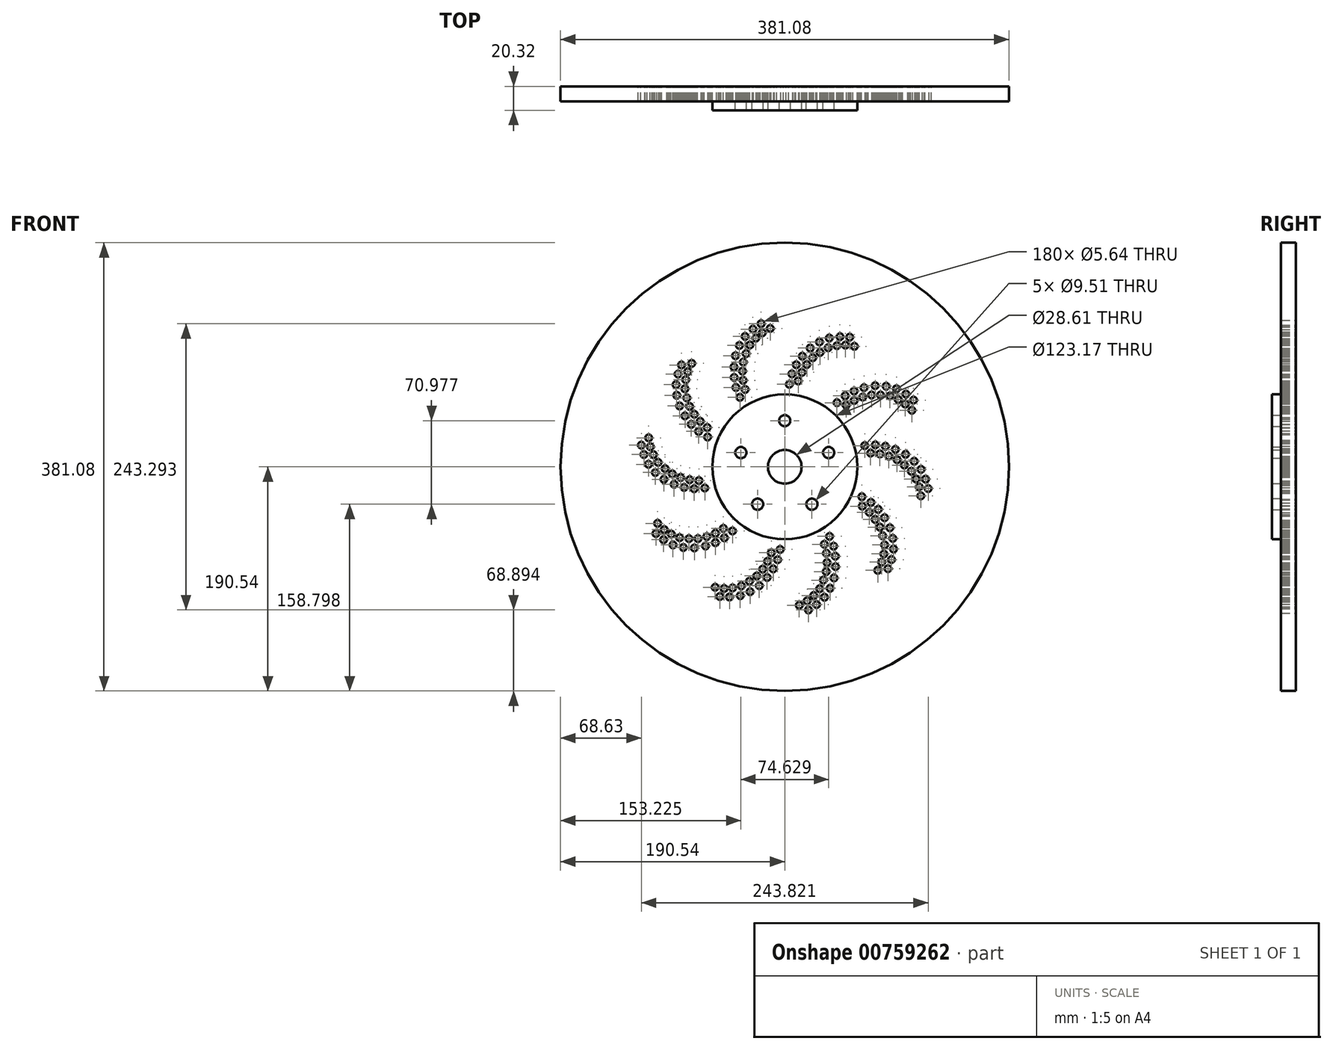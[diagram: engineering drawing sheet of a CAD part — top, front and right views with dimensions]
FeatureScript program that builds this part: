
annotation { "Feature Type Name" : "Feature", "Feature Type Description" : "" }
export const myFeature = defineFeature(function(context is Context, id is Id, definition is map)
    precondition{}
    {
        {
            var Q0;
            Q0=qCreatedBy(makeId("Front.planeOp"),FACE);
            var sketch = newSketch(context, id + "F0", { "sketchPlane" : qUnion([Q0])});
            skCircle(sketch, "E0", {"center": v(0, 0) * mm, "radius": 190.54 * mm});
            skCircle(sketch, "E1", {"center": v(0, 39.24) * mm, "radius": 4.75 * mm});
            skCircle(sketch, "E2.1.0", {"center": v(37.32, 12.13) * mm, "radius": 4.75 * mm});
            skCircle(sketch, "E2.2.0", {"center": v(23.06, -31.74) * mm, "radius": 4.75 * mm});
            skCircle(sketch, "E2.3.0", {"center": v(-23.06, -31.74) * mm, "radius": 4.75 * mm});
            skCircle(sketch, "E2.4.0", {"center": v(-37.31, 12.13) * mm, "radius": 4.75 * mm});
            skCircle(sketch, "E3", {"center": v(0, 0) * mm, "radius": 14.3 * mm});
            skCircle(sketch, "E4", {"center": v(0, 0) * mm, "radius": 61.59 * mm});
            skCircle(sketch, "E5", {"center": v(-38.12, 59.08) * mm, "radius": 2.82 * mm});
            skCircle(sketch, "E6.1.0", {"center": v(3.89, 70.2) * mm, "radius": 2.82 * mm});
            skCircle(sketch, "E6.2.0", {"center": v(44.4, 54.51) * mm, "radius": 2.82 * mm});
            skCircle(sketch, "E6.3.0", {"center": v(67.97, 18) * mm, "radius": 2.82 * mm});
            skCircle(sketch, "E6.4.0", {"center": v(65.57, -25.4) * mm, "radius": 2.82 * mm});
            skCircle(sketch, "E6.5.0", {"center": v(38.12, -59.08) * mm, "radius": 2.82 * mm});
            skCircle(sketch, "E6.6.0", {"center": v(-3.89, -70.2) * mm, "radius": 2.82 * mm});
            skCircle(sketch, "E6.7.0", {"center": v(-44.4, -54.51) * mm, "radius": 2.82 * mm});
            skCircle(sketch, "E6.8.0", {"center": v(-67.97, -18) * mm, "radius": 2.82 * mm});
            skCircle(sketch, "E6.9.0", {"center": v(-65.57, 25.4) * mm, "radius": 2.82 * mm});
            skLineSegment(sketch, "E6.anchor1", {"start": v(0, 0) * mm, "end": v(-38.12, 59.08) * mm, "construction": true});
            skLineSegment(sketch, "E6.anchor2", {"start": v(0, 0) * mm, "end": v(-65.57, 25.4) * mm, "construction": true});
            skLineSegment(sketch, "E7.anchor1", {"start": v(0, 0) * mm, "end": v(3.89, 70.2) * mm, "construction": true});
            skCircle(sketch, "E8.9.0", {"center": v(-41.5, 67.47) * mm, "radius": 2.82 * mm});
            skCircle(sketch, "E9.1.0", {"center": v(-73.23, 30.19) * mm, "radius": 2.82 * mm});
            skCircle(sketch, "E9.2.0", {"center": v(-77, -18.63) * mm, "radius": 2.82 * mm});
            skCircle(sketch, "E9.3.0", {"center": v(-51.34, -60.32) * mm, "radius": 2.82 * mm});
            skCircle(sketch, "E9.4.0", {"center": v(-6.08, -78.98) * mm, "radius": 2.82 * mm});
            skCircle(sketch, "E9.5.0", {"center": v(41.5, -67.47) * mm, "radius": 2.82 * mm});
            skCircle(sketch, "E9.6.0", {"center": v(73.23, -30.19) * mm, "radius": 2.82 * mm});
            skCircle(sketch, "E9.7.0", {"center": v(77, 18.63) * mm, "radius": 2.82 * mm});
            skCircle(sketch, "E9.8.0", {"center": v(51.34, 60.32) * mm, "radius": 2.82 * mm});
            skCircle(sketch, "E9.9.0", {"center": v(6.08, 78.98) * mm, "radius": 2.82 * mm});
            skCircle(sketch, "E10.9.0", {"center": v(-43.06, 75.98) * mm, "radius": 2.82 * mm});
            skCircle(sketch, "E11.1.0", {"center": v(-79.5, 36.16) * mm, "radius": 2.82 * mm});
            skCircle(sketch, "E11.2.0", {"center": v(-85.56, -17.47) * mm, "radius": 2.82 * mm});
            skCircle(sketch, "E11.3.0", {"center": v(-58.95, -64.43) * mm, "radius": 2.82 * mm});
            skCircle(sketch, "E11.4.0", {"center": v(-9.83, -86.78) * mm, "radius": 2.82 * mm});
            skCircle(sketch, "E11.5.0", {"center": v(43.06, -75.98) * mm, "radius": 2.82 * mm});
            skCircle(sketch, "E11.6.0", {"center": v(79.5, -36.16) * mm, "radius": 2.82 * mm});
            skCircle(sketch, "E11.7.0", {"center": v(85.56, 17.47) * mm, "radius": 2.82 * mm});
            skCircle(sketch, "E11.8.0", {"center": v(58.95, 64.43) * mm, "radius": 2.82 * mm});
            skCircle(sketch, "E11.9.0", {"center": v(9.83, 86.78) * mm, "radius": 2.82 * mm});
            skCircle(sketch, "E12.9.0", {"center": v(-43.16, 84.86) * mm, "radius": 2.82 * mm});
            skCircle(sketch, "E13.1.0", {"center": v(-84.8, 43.28) * mm, "radius": 2.82 * mm});
            skCircle(sketch, "E13.2.0", {"center": v(-94.04, -14.82) * mm, "radius": 2.82 * mm});
            skCircle(sketch, "E13.3.0", {"center": v(-67.37, -67.27) * mm, "radius": 2.82 * mm});
            skCircle(sketch, "E13.4.0", {"center": v(-14.96, -94.02) * mm, "radius": 2.82 * mm});
            skCircle(sketch, "E13.5.0", {"center": v(43.16, -84.86) * mm, "radius": 2.82 * mm});
            skCircle(sketch, "E13.6.0", {"center": v(84.8, -43.28) * mm, "radius": 2.82 * mm});
            skCircle(sketch, "E13.7.0", {"center": v(94.04, 14.82) * mm, "radius": 2.82 * mm});
            skCircle(sketch, "E13.8.0", {"center": v(67.37, 67.27) * mm, "radius": 2.82 * mm});
            skCircle(sketch, "E13.9.0", {"center": v(14.96, 94.02) * mm, "radius": 2.82 * mm});
            skCircle(sketch, "E14.9.0", {"center": v(-41.86, 94.41) * mm, "radius": 2.82 * mm});
            skCircle(sketch, "E15.9.0", {"center": v(-38.55, 103.18) * mm, "radius": 2.82 * mm});
            skCircle(sketch, "E16.1.0", {"center": v(-91.84, 60.81) * mm, "radius": 2.82 * mm});
            skCircle(sketch, "E16.2.0", {"center": v(-110.04, -4.78) * mm, "radius": 2.82 * mm});
            skCircle(sketch, "E16.3.0", {"center": v(-86.22, -68.55) * mm, "radius": 2.82 * mm});
            skCircle(sketch, "E16.4.0", {"center": v(-29.46, -106.13) * mm, "radius": 2.82 * mm});
            skCircle(sketch, "E16.5.0", {"center": v(38.55, -103.18) * mm, "radius": 2.82 * mm});
            skCircle(sketch, "E16.6.0", {"center": v(91.84, -60.81) * mm, "radius": 2.82 * mm});
            skCircle(sketch, "E16.7.0", {"center": v(110.04, 4.78) * mm, "radius": 2.82 * mm});
            skCircle(sketch, "E16.8.0", {"center": v(86.22, 68.55) * mm, "radius": 2.82 * mm});
            skCircle(sketch, "E16.9.0", {"center": v(29.46, 106.13) * mm, "radius": 2.82 * mm});
            skCircle(sketch, "E17.1.0", {"center": v(-89.36, 51.78) * mm, "radius": 2.82 * mm});
            skCircle(sketch, "E17.2.0", {"center": v(-102.73, -10.64) * mm, "radius": 2.82 * mm});
            skCircle(sketch, "E17.3.0", {"center": v(-76.86, -68.99) * mm, "radius": 2.82 * mm});
            skCircle(sketch, "E17.4.0", {"center": v(-21.63, -100.99) * mm, "radius": 2.82 * mm});
            skCircle(sketch, "E17.5.0", {"center": v(41.86, -94.41) * mm, "radius": 2.82 * mm});
            skCircle(sketch, "E17.6.0", {"center": v(89.36, -51.78) * mm, "radius": 2.82 * mm});
            skCircle(sketch, "E17.7.0", {"center": v(102.73, 10.64) * mm, "radius": 2.82 * mm});
            skCircle(sketch, "E17.8.0", {"center": v(76.86, 68.99) * mm, "radius": 2.82 * mm});
            skCircle(sketch, "E17.9.0", {"center": v(21.63, 100.99) * mm, "radius": 2.82 * mm});
            skCircle(sketch, "E18.9.0", {"center": v(-33.74, 110.84) * mm, "radius": 2.82 * mm});
            skCircle(sketch, "E19.1.0", {"center": v(-92.45, 69.84) * mm, "radius": 2.82 * mm});
            skCircle(sketch, "E19.2.0", {"center": v(-115.84, 2.16) * mm, "radius": 2.82 * mm});
            skCircle(sketch, "E19.3.0", {"center": v(-94.99, -66.34) * mm, "radius": 2.82 * mm});
            skCircle(sketch, "E19.4.0", {"center": v(-37.85, -109.5) * mm, "radius": 2.82 * mm});
            skCircle(sketch, "E19.5.0", {"center": v(33.74, -110.84) * mm, "radius": 2.82 * mm});
            skCircle(sketch, "E19.6.0", {"center": v(92.45, -69.84) * mm, "radius": 2.82 * mm});
            skCircle(sketch, "E19.7.0", {"center": v(115.84, -2.16) * mm, "radius": 2.82 * mm});
            skCircle(sketch, "E19.8.0", {"center": v(94.99, 66.34) * mm, "radius": 2.82 * mm});
            skCircle(sketch, "E19.9.0", {"center": v(37.85, 109.5) * mm, "radius": 2.82 * mm});
            skCircle(sketch, "E20.9.0", {"center": v(-27.05, 117.1) * mm, "radius": 2.82 * mm});
            skCircle(sketch, "E21.1.0", {"center": v(-90.7, 78.84) * mm, "radius": 2.82 * mm});
            skCircle(sketch, "E21.2.0", {"center": v(-119.72, 10.46) * mm, "radius": 2.82 * mm});
            skCircle(sketch, "E21.3.0", {"center": v(-103, -61.9) * mm, "radius": 2.82 * mm});
            skCircle(sketch, "E21.4.0", {"center": v(-46.95, -110.63) * mm, "radius": 2.82 * mm});
            skCircle(sketch, "E21.5.0", {"center": v(27.05, -117.1) * mm, "radius": 2.82 * mm});
            skCircle(sketch, "E21.6.0", {"center": v(90.7, -78.84) * mm, "radius": 2.82 * mm});
            skCircle(sketch, "E21.7.0", {"center": v(119.72, -10.46) * mm, "radius": 2.82 * mm});
            skCircle(sketch, "E21.8.0", {"center": v(103, 61.9) * mm, "radius": 2.82 * mm});
            skCircle(sketch, "E21.9.0", {"center": v(46.95, 110.63) * mm, "radius": 2.82 * mm});
            skCircle(sketch, "E22.9.0", {"center": v(-20.12, 121.65) * mm, "radius": 2.82 * mm});
            skCircle(sketch, "E23.1.0", {"center": v(-87.78, 86.59) * mm, "radius": 2.82 * mm});
            skCircle(sketch, "E23.2.0", {"center": v(-121.91, 18.45) * mm, "radius": 2.82 * mm});
            skCircle(sketch, "E23.3.0", {"center": v(-109.47, -56.73) * mm, "radius": 2.82 * mm});
            skCircle(sketch, "E23.4.0", {"center": v(-55.22, -110.24) * mm, "radius": 2.82 * mm});
            skCircle(sketch, "E23.5.0", {"center": v(20.12, -121.65) * mm, "radius": 2.82 * mm});
            skCircle(sketch, "E23.6.0", {"center": v(87.78, -86.59) * mm, "radius": 2.82 * mm});
            skCircle(sketch, "E23.7.0", {"center": v(121.91, -18.45) * mm, "radius": 2.82 * mm});
            skCircle(sketch, "E23.8.0", {"center": v(109.47, 56.73) * mm, "radius": 2.82 * mm});
            skCircle(sketch, "E23.9.0", {"center": v(55.22, 110.24) * mm, "radius": 2.82 * mm});
            skCircle(sketch, "E24.9.0", {"center": v(-33.66, 65.79) * mm, "radius": 2.82 * mm});
            skCircle(sketch, "E25.9.0", {"center": v(-35.41, 73.5) * mm, "radius": 2.82 * mm});
            skCircle(sketch, "E26.9.0", {"center": v(-35.92, 81.34) * mm, "radius": 2.82 * mm});
            skCircle(sketch, "E27.9.0", {"center": v(-35.26, 89) * mm, "radius": 2.82 * mm});
            skCircle(sketch, "E28.9.0", {"center": v(-32.86, 96.27) * mm, "radius": 2.82 * mm});
            skCircle(sketch, "E29.9.0", {"center": v(-29.65, 103.57) * mm, "radius": 2.82 * mm});
            skCircle(sketch, "E30.9.0", {"center": v(-24.62, 109.4) * mm, "radius": 2.82 * mm});
            skCircle(sketch, "E31.9.0", {"center": v(-19.06, 113.94) * mm, "radius": 2.82 * mm});
            skCircle(sketch, "E32.9.0", {"center": v(-12.3, 117.63) * mm, "radius": 2.82 * mm});
            skCircle(sketch, "E33.1.0", {"center": v(-65.9, 33.44) * mm, "radius": 2.82 * mm});
            skCircle(sketch, "E33.2.0", {"center": v(-72.97, -11.68) * mm, "radius": 2.82 * mm});
            skCircle(sketch, "E33.3.0", {"center": v(-52.17, -52.34) * mm, "radius": 2.82 * mm});
            skCircle(sketch, "E33.4.0", {"center": v(-11.44, -73) * mm, "radius": 2.82 * mm});
            skCircle(sketch, "E33.5.0", {"center": v(33.66, -65.79) * mm, "radius": 2.82 * mm});
            skCircle(sketch, "E33.6.0", {"center": v(65.9, -33.44) * mm, "radius": 2.82 * mm});
            skCircle(sketch, "E33.7.0", {"center": v(72.97, 11.68) * mm, "radius": 2.82 * mm});
            skCircle(sketch, "E33.8.0", {"center": v(52.17, 52.34) * mm, "radius": 2.82 * mm});
            skCircle(sketch, "E33.9.0", {"center": v(11.44, 73) * mm, "radius": 2.82 * mm});
            skCircle(sketch, "E34.1.0", {"center": v(-71.85, 38.65) * mm, "radius": 2.82 * mm});
            skCircle(sketch, "E34.2.0", {"center": v(-80.84, -10.97) * mm, "radius": 2.82 * mm});
            skCircle(sketch, "E34.3.0", {"center": v(-58.96, -56.39) * mm, "radius": 2.82 * mm});
            skCircle(sketch, "E34.4.0", {"center": v(-14.55, -80.27) * mm, "radius": 2.82 * mm});
            skCircle(sketch, "E34.5.0", {"center": v(35.41, -73.5) * mm, "radius": 2.82 * mm});
            skCircle(sketch, "E34.6.0", {"center": v(71.85, -38.65) * mm, "radius": 2.82 * mm});
            skCircle(sketch, "E34.7.0", {"center": v(80.84, 10.97) * mm, "radius": 2.82 * mm});
            skCircle(sketch, "E34.8.0", {"center": v(58.96, 56.39) * mm, "radius": 2.82 * mm});
            skCircle(sketch, "E34.9.0", {"center": v(14.55, 80.27) * mm, "radius": 2.82 * mm});
            skCircle(sketch, "E35.1.0", {"center": v(-76.87, 44.69) * mm, "radius": 2.82 * mm});
            skCircle(sketch, "E35.2.0", {"center": v(-88.46, -9.03) * mm, "radius": 2.82 * mm});
            skCircle(sketch, "E35.3.0", {"center": v(-66.26, -59.3) * mm, "radius": 2.82 * mm});
            skCircle(sketch, "E35.4.0", {"center": v(-18.75, -86.92) * mm, "radius": 2.82 * mm});
            skCircle(sketch, "E35.5.0", {"center": v(35.92, -81.34) * mm, "radius": 2.82 * mm});
            skCircle(sketch, "E35.6.0", {"center": v(76.87, -44.69) * mm, "radius": 2.82 * mm});
            skCircle(sketch, "E35.7.0", {"center": v(88.46, 9.03) * mm, "radius": 2.82 * mm});
            skCircle(sketch, "E35.8.0", {"center": v(66.26, 59.3) * mm, "radius": 2.82 * mm});
            skCircle(sketch, "E35.9.0", {"center": v(18.75, 86.92) * mm, "radius": 2.82 * mm});
            skCircle(sketch, "E36.1.0", {"center": v(-83.17, 58.57) * mm, "radius": 2.82 * mm});
            skCircle(sketch, "E36.1.1", {"center": v(-80.84, 51.29) * mm, "radius": 2.82 * mm});
            skCircle(sketch, "E36.1.2", {"center": v(-84.21, 74.03) * mm, "radius": 2.82 * mm});
            skCircle(sketch, "E36.1.3", {"center": v(-84.86, 66.36) * mm, "radius": 2.82 * mm});
            skCircle(sketch, "E36.2.0", {"center": v(-101.71, -1.5) * mm, "radius": 2.82 * mm});
            skCircle(sketch, "E36.2.1", {"center": v(-95.55, -6.02) * mm, "radius": 2.82 * mm});
            skCircle(sketch, "E36.2.2", {"center": v(-111.64, 10.4) * mm, "radius": 2.82 * mm});
            skCircle(sketch, "E36.2.3", {"center": v(-107.66, 3.8) * mm, "radius": 2.82 * mm});
            skCircle(sketch, "E36.3.0", {"center": v(-81.4, -61) * mm, "radius": 2.82 * mm});
            skCircle(sketch, "E36.3.1", {"center": v(-73.76, -61.04) * mm, "radius": 2.82 * mm});
            skCircle(sketch, "E36.3.2", {"center": v(-96.43, -57.22) * mm, "radius": 2.82 * mm});
            skCircle(sketch, "E36.3.3", {"center": v(-89.34, -60.2) * mm, "radius": 2.82 * mm});
            skCircle(sketch, "E36.4.0", {"center": v(-30, -97.2) * mm, "radius": 2.82 * mm});
            skCircle(sketch, "E36.4.1", {"center": v(-23.8, -92.73) * mm, "radius": 2.82 * mm});
            skCircle(sketch, "E36.4.2", {"center": v(-44.38, -102.97) * mm, "radius": 2.82 * mm});
            skCircle(sketch, "E36.4.3", {"center": v(-36.9, -101.22) * mm, "radius": 2.82 * mm});
            skCircle(sketch, "E36.5.0", {"center": v(32.86, -96.27) * mm, "radius": 2.82 * mm});
            skCircle(sketch, "E36.5.1", {"center": v(35.26, -89) * mm, "radius": 2.82 * mm});
            skCircle(sketch, "E36.5.2", {"center": v(24.62, -109.4) * mm, "radius": 2.82 * mm});
            skCircle(sketch, "E36.5.3", {"center": v(29.65, -103.57) * mm, "radius": 2.82 * mm});
            skCircle(sketch, "E36.6.0", {"center": v(83.17, -58.57) * mm, "radius": 2.82 * mm});
            skCircle(sketch, "E36.6.1", {"center": v(80.84, -51.29) * mm, "radius": 2.82 * mm});
            skCircle(sketch, "E36.6.2", {"center": v(84.21, -74.03) * mm, "radius": 2.82 * mm});
            skCircle(sketch, "E36.6.3", {"center": v(84.86, -66.36) * mm, "radius": 2.82 * mm});
            skCircle(sketch, "E36.7.0", {"center": v(101.71, 1.5) * mm, "radius": 2.82 * mm});
            skCircle(sketch, "E36.7.1", {"center": v(95.55, 6.02) * mm, "radius": 2.82 * mm});
            skCircle(sketch, "E36.7.2", {"center": v(111.64, -10.4) * mm, "radius": 2.82 * mm});
            skCircle(sketch, "E36.7.3", {"center": v(107.66, -3.8) * mm, "radius": 2.82 * mm});
            skCircle(sketch, "E36.8.0", {"center": v(81.4, 61) * mm, "radius": 2.82 * mm});
            skCircle(sketch, "E36.8.1", {"center": v(73.76, 61.04) * mm, "radius": 2.82 * mm});
            skCircle(sketch, "E36.8.2", {"center": v(96.43, 57.22) * mm, "radius": 2.82 * mm});
            skCircle(sketch, "E36.8.3", {"center": v(89.34, 60.2) * mm, "radius": 2.82 * mm});
            skCircle(sketch, "E36.9.0", {"center": v(30, 97.2) * mm, "radius": 2.82 * mm});
            skCircle(sketch, "E36.9.1", {"center": v(23.8, 92.73) * mm, "radius": 2.82 * mm});
            skCircle(sketch, "E36.9.2", {"center": v(44.38, 102.97) * mm, "radius": 2.82 * mm});
            skCircle(sketch, "E36.9.3", {"center": v(36.9, 101.22) * mm, "radius": 2.82 * mm});
            skCircle(sketch, "E37.1.2", {"center": v(-82.39, 80.98) * mm, "radius": 2.82 * mm});
            skCircle(sketch, "E37.1.3", {"center": v(-79.1, 87.93) * mm, "radius": 2.82 * mm});
            skCircle(sketch, "E37.2.2", {"center": v(-114.25, 17.09) * mm, "radius": 2.82 * mm});
            skCircle(sketch, "E37.2.3", {"center": v(-115.67, 24.65) * mm, "radius": 2.82 * mm});
            skCircle(sketch, "E37.3.2", {"center": v(-102.47, -53.33) * mm, "radius": 2.82 * mm});
            skCircle(sketch, "E37.3.3", {"center": v(-108.07, -48.05) * mm, "radius": 2.82 * mm});
            skCircle(sketch, "E37.4.2", {"center": v(-51.55, -103.38) * mm, "radius": 2.82 * mm});
            skCircle(sketch, "E37.4.3", {"center": v(-59.18, -102.4) * mm, "radius": 2.82 * mm});
            skCircle(sketch, "E37.5.2", {"center": v(19.06, -113.94) * mm, "radius": 2.82 * mm});
            skCircle(sketch, "E37.5.3", {"center": v(12.3, -117.63) * mm, "radius": 2.82 * mm});
            skCircle(sketch, "E37.6.2", {"center": v(82.39, -80.98) * mm, "radius": 2.82 * mm});
            skCircle(sketch, "E37.6.3", {"center": v(79.1, -87.93) * mm, "radius": 2.82 * mm});
            skCircle(sketch, "E37.7.2", {"center": v(114.25, -17.09) * mm, "radius": 2.82 * mm});
            skCircle(sketch, "E37.7.3", {"center": v(115.67, -24.65) * mm, "radius": 2.82 * mm});
            skCircle(sketch, "E37.8.2", {"center": v(102.47, 53.33) * mm, "radius": 2.82 * mm});
            skCircle(sketch, "E37.8.3", {"center": v(108.07, 48.05) * mm, "radius": 2.82 * mm});
            skCircle(sketch, "E37.9.2", {"center": v(51.55, 103.38) * mm, "radius": 2.82 * mm});
            skCircle(sketch, "E37.9.3", {"center": v(59.18, 102.4) * mm, "radius": 2.82 * mm});
            skSolve(sketch);
        }
        {
            var Q0;
            Q0 = qSketchRegion(id + "F0", true);
            extrude(context, id + "F1", {"entities" : qUnion([Q0]), "depth" : 12.7 * mm, "offsetDistance" : 25.4 * mm});
        }
        {
            var Q0;
            Q0=makeQuery(id+"F1.opExtrude","CAP_FACE",FACE,{"disambiguationData":[OSD([sQuery(id+"F0.wireOp",EDGE,"E0")])],"isStart":false});
            var sketch = newSketch(context, id + "F2", { "sketchPlane" : qUnion([Q0])});
            skCircle(sketch, "E38", {"center": v(0, 0) * mm, "radius": 61.59 * mm});
            skCircle(sketch, "E39", {"center": v(0, 39.23) * mm, "radius": 4.75 * mm});
            skCircle(sketch, "E40.1.0", {"center": v(37.31, 12.12) * mm, "radius": 4.75 * mm});
            skCircle(sketch, "E40.2.0", {"center": v(23.06, -31.74) * mm, "radius": 4.75 * mm});
            skCircle(sketch, "E40.3.0", {"center": v(-23.06, -31.74) * mm, "radius": 4.75 * mm});
            skCircle(sketch, "E40.4.0", {"center": v(-37.31, 12.12) * mm, "radius": 4.75 * mm});
            skLineSegment(sketch, "E40.anchor1", {"start": v(0, 0) * mm, "end": v(0, 39.23) * mm, "construction": true});
            skLineSegment(sketch, "E40.anchor2", {"start": v(0, 0) * mm, "end": v(-37.31, 12.12) * mm, "construction": true});
            skCircle(sketch, "E41", {"center": v(0, 0) * mm, "radius": 14.3 * mm});
            skSolve(sketch);
        }
        {
            var Q0;
            Q0 = qSketchRegion(id + "F2", true);
            extrude(context, id + "F3", {"entities" : qUnion([Q0]), "operationType" : NewBodyOperationType.ADD, "depth" : 7.62 * mm, "offsetDistance" : 25.4 * mm});
        }
    });
